# Revit family: Domotics-DomesticRanges-GEWISS-CHORUS_SIGNALLING-LAMP_DOPPIE_1M
name_source: partatom
category: Apparecchi elettrici
revit_build: Autodesk Revit 2016 (Build: 20161004_0715(x64)
units: mm (PartAtom-declared; Revit-internal decimal feet)

## family parameters
Condiviso = Sì
Host = Superficie
Mantenere orientamento annotazione = Sì
Punto di calcolo locali = Sì
Quota connettore circolare = Usa diametro
Taglio con vuoti quando caricato = Sì
Tipo di parte = Normale

## types (6) — shared parameters
Catalogue = DOMOTICS
Catalogue Range = CHORUS - DOMESTIC RANGE
Description. = Double flat indicator lamp
Electrocod = 0132
IDF = 08717724-49fc-4206-85ed-fa04fe0284d9
IDT = d8a86530-3b18-4f53-a409-0b95887879fe
Immagine tipo = GW14629.jpg
No. Chorus modules = 1
No. Chorus modules: = 1
Produttore = GEWISS S.p.A.
Prospetto di default = 1219 mm
SEO = Indicator
Signalling unit = With wired lead
Technical sheet = https://www.gewiss.com
Tipo_ = Chorus Spie Doppie 1M_GENERICO : GW14629 Spia di segnalazione doppia rosso/verde titanio
URL = https://www.gewiss.com
Version file RFA = 19.0

## per-type parameters (varying)
| type | Colour | Descrizione | Diffuser colour | EAN code | Modello |
| GW14629 - Double red/grn indicator lamp, titanium | Titanium | DOUBLE RED/GRN INDICATOR LAMP, TITANIUM | Red/green | 8011564268531 | GW14629 |
| GW10629 - Double red/green indicator lamp, white | White | DOUBLE RED/GREEN INDICATOR LAMP, WHITE | Red/green | 8011564259652 | GW10629 |
| GW12629 - Double red/green indicator lamp, black | Black | DOUBLE RED/GREEN INDICATOR LAMP, BLACK | Red/green | 8011564269286 | GW12629 |
| GW12628 - Double transparent indicator lamp, black | Black | DOUBLE TRANSPARENT INDICATOR LAMP, BLACK | Opal | 8011564269279 | GW12628 |
| GW14628 - Double transp indicator lamp, titanium | Titanium | DOUBLE TRANSP INDICATOR LAMP, TITANIUM | Opal | 8011564268524 | GW14628 |
| GW10628 - Double transparent indicator lamp, white | White | DOUBLE TRANSPARENT INDICATOR LAMP, WHITE | Opal | 8011564259645 | GW10628 |

## geometry (parser evidence)
native form markers: Sweep x2
no freeform markers — native parametric forms only
